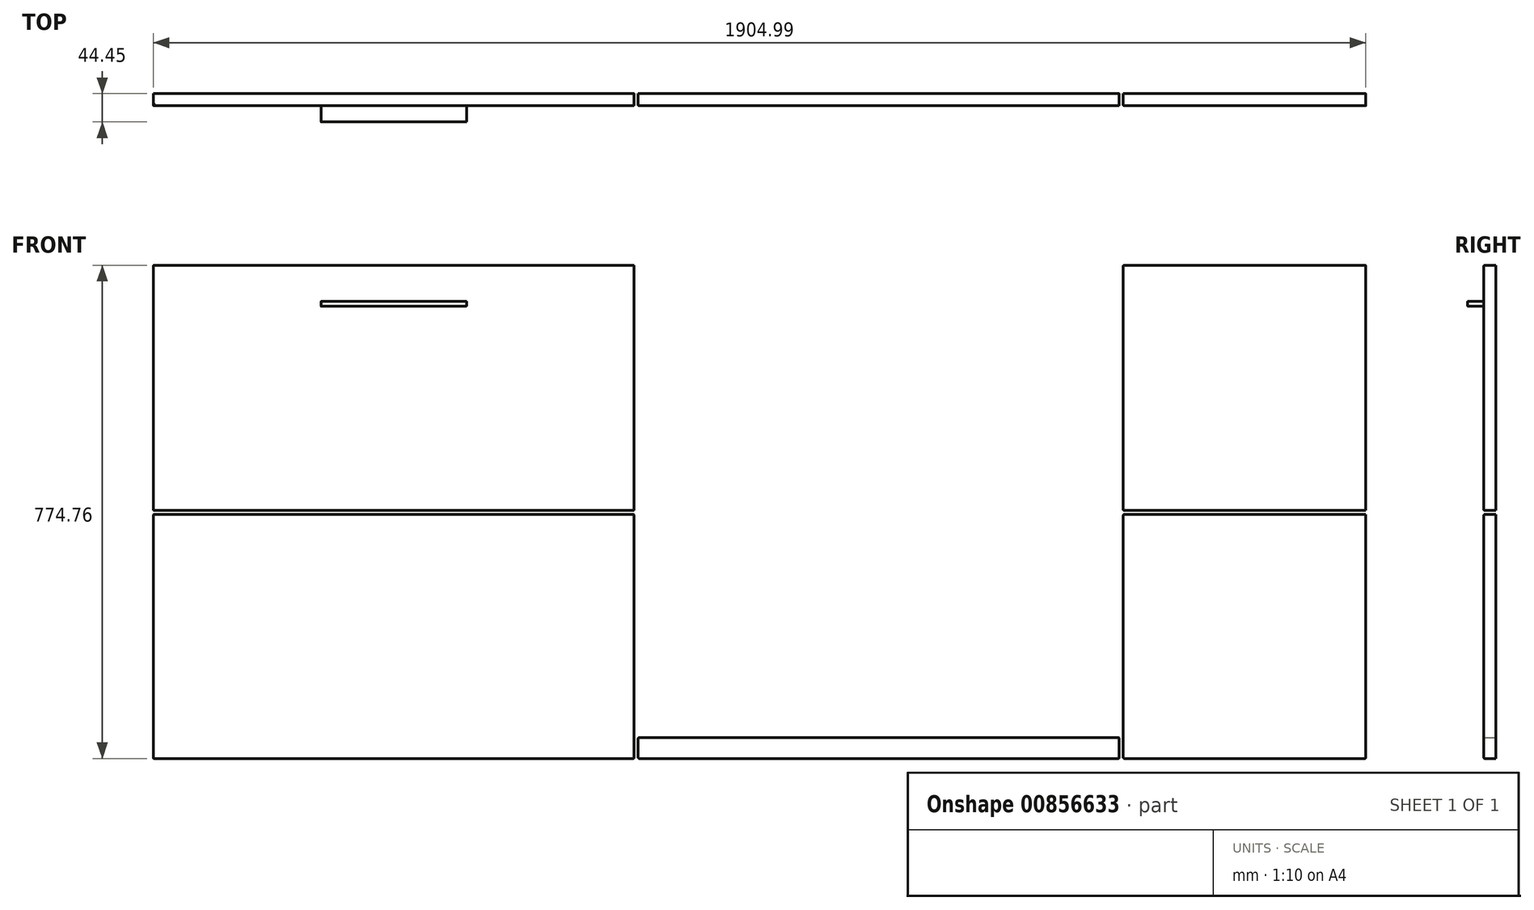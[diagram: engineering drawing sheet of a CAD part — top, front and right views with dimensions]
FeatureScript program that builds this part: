
annotation { "Feature Type Name" : "Feature", "Feature Type Description" : "" }
export const myFeature = defineFeature(function(context is Context, id is Id, definition is map)
    precondition{}
    {
        {
            var Q0;
            Q0=qCreatedBy(makeId("Front.planeOp"),FACE);
            var sketch = newSketch(context, id + "F0", { "sketchPlane" : qUnion([Q0])});
            skLineSegment(sketch, "E0.left", {"start": v(0, 0) * mm, "end": v(0.1, 863.6) * mm});
            skLineSegment(sketch, "E0.right", {"start": v(-1905, -2.15) * mm, "end": v(-1904.9, 861.45) * mm});
            skLineSegment(sketch, "E1.top", {"start": v(0.1, 901.7) * mm, "end": v(-2504.34, 901.7) * mm});
            skLineSegment(sketch, "E1.left", {"start": v(0.1, 863.6) * mm, "end": v(0.1, 901.7) * mm});
            skLineSegment(sketch, "E1.right", {"start": v(-2504.34, 863.6) * mm, "end": v(-2504.34, 901.7) * mm});
            skLineSegment(sketch, "E2", {"start": v(-1904.9, 1058.57) * mm, "end": v(-1904.9, -228.77) * mm, "construction": true});
            skLineSegment(sketch, "E3", {"start": v(0, 1058.57) * mm, "end": v(0, -228.77) * mm, "construction": true});
            skLineSegment(sketch, "E4.bottom", {"start": v(0, 0) * mm, "end": v(-381, 0) * mm});
            skLineSegment(sketch, "E4.left", {"start": v(0, 0) * mm, "end": v(0, 857.25) * mm});
            skLineSegment(sketch, "E5", {"start": v(-381, 0) * mm, "end": v(-387.35, 0) * mm, "construction": true});
            skLineSegment(sketch, "E6.bottom", {"start": v(-387.35, 0) * mm, "end": v(-1143, 0) * mm, "construction": true});
            skLineSegment(sketch, "E6.left", {"start": v(-387.35, 0) * mm, "end": v(-387.35, 736.6) * mm, "construction": true});
            skLineSegment(sketch, "E7", {"start": v(0, 0) * mm, "end": v(-1905, -2.15) * mm, "construction": true});
            skLineSegment(sketch, "E8.bottom", {"start": v(-387.35, 857.25) * mm, "end": v(-1143, 857.25) * mm, "construction": true});
            skLineSegment(sketch, "E8.top", {"start": v(-387.35, 121.5) * mm, "end": v(-1143, 120.65) * mm, "construction": true});
            skLineSegment(sketch, "E8.left", {"start": v(-387.35, 857.25) * mm, "end": v(-387.35, 121.5) * mm, "construction": true});
            skLineSegment(sketch, "E8.right", {"start": v(-1143, 857.25) * mm, "end": v(-1143, 120.65) * mm, "construction": true});
            skLineSegment(sketch, "E9", {"start": v(-1149.35, 857.25) * mm, "end": v(-1149.35, 120.65) * mm, "construction": true});
            skLineSegment(sketch, "E10.bottom", {"start": v(-1149.35, 857.25) * mm, "end": v(-1527.18, 857.25) * mm});
            skLineSegment(sketch, "E10.left", {"start": v(-1149.35, 857.25) * mm, "end": v(-1149.35, 82.55) * mm});
            skLineSegment(sketch, "E11.bottom", {"start": v(-1149.35, 82.5) * mm, "end": v(-1911.35, 82.5) * mm});
            skLineSegment(sketch, "E11.top", {"start": v(-1149.35, 857.25) * mm, "end": v(-1911.35, 857.25) * mm});
            skLineSegment(sketch, "E11.left", {"start": v(-1149.35, 82.5) * mm, "end": v(-1149.35, 857.25) * mm});
            skLineSegment(sketch, "E11.right", {"start": v(-1911.35, 82.5) * mm, "end": v(-1911.35, 857.25) * mm});
            skLineSegment(sketch, "E12", {"start": v(0, 857.25) * mm, "end": v(-2682.58, 857.25) * mm, "construction": true});
            skLineSegment(sketch, "E13.bottom", {"start": v(0, 857.25) * mm, "end": v(-381, 857.25) * mm});
            skLineSegment(sketch, "E13.top", {"start": v(0, 82.55) * mm, "end": v(-381, 82.55) * mm});
            skLineSegment(sketch, "E13.left", {"start": v(0, 857.25) * mm, "end": v(0, 82.55) * mm});
            skLineSegment(sketch, "E13.right", {"start": v(-381, 857.25) * mm, "end": v(-381, 82.55) * mm});
            skLineSegment(sketch, "E14.bottom", {"start": v(-387.35, 82.55) * mm, "end": v(-1143, 82.55) * mm});
            skLineSegment(sketch, "E14.top", {"start": v(-387.35, 115.22) * mm, "end": v(-1143, 115.22) * mm});
            skLineSegment(sketch, "E14.left", {"start": v(-387.35, 82.55) * mm, "end": v(-387.35, 115.22) * mm});
            skLineSegment(sketch, "E14.right", {"start": v(-1143, 82.55) * mm, "end": v(-1143, 115.22) * mm});
            skPoint(sketch, "E15", {"position": v(-765.18, 121.08) * mm});
            skSolve(sketch);
        }
        {
            var Q0;
            {var subQ0=sQuery(id+"F0.wireOp",EDGE,"E0.left");Q0=makeQuery(id+"F0.imprint","IMPRINT",FACE,{"disambiguationData":[TD([[makeQuery(id+"F0.imprint","IMPRINT",EDGE,{"derivedFrom":subQ0}),1.0]])]});}
            var Q1;
            Q1=makeQuery(id+"F0.imprint","IMPRINT",FACE,{"disambiguationData":[TD([[makeQuery(id+"F0.imprint","IMPRINT",EDGE,{"derivedFrom":sQuery(id+"F0.wireOp",EDGE,"E13.bottom")}),1.0]])]});
            var Q2;
            Q2=makeQuery(id+"F0.imprint","IMPRINT",FACE,{"disambiguationData":[TD([[makeQuery(id+"F0.imprint","IMPRINT",EDGE,{"derivedFrom":sQuery(id+"F0.wireOp",EDGE,"E10.bottom")}),1.0]])]});
            var Q3;
            {var subQ5=sQuery(id+"F0.wireOp",EDGE,"E11.left");Q3=makeQuery(id+"F0.imprint","IMPRINT",FACE,{"disambiguationData":[TD([[makeQuery(id+"F0.imprint","IMPRINT",EDGE,{"derivedFrom":subQ5}),1.0]])]});}
            var Q4;
            Q4=makeQuery(id+"F0.imprint","IMPRINT",FACE,{"disambiguationData":[TD([[makeQuery(id+"F0.imprint","IMPRINT",EDGE,{"derivedFrom":sQuery(id+"F0.wireOp",EDGE,"E14.bottom")}),-1.0]])]});
            extrude(context, id + "F1", {"entities" : qUnion([Q0, Q1, Q2, Q3, Q4]), "depth" : 19.05 * mm, "offsetDistance" : 25.4 * mm});
        }
        {
            var Q0;
            Q0=makeQuery(id+"F1.opExtrude","CAP_EDGE",EDGE,{"disambiguationData":[OSD([sQuery(id+"F0.wireOp",EDGE,"E10.bottom")])],"isStart":false});
            var Q1;
            Q1=makeQuery(id+"F1.opExtrude","SWEPT_EDGE",EDGE,{"disambiguationData":[OSD([sQuery(id+"F0.wireOp",EDGE,"E10.bottom"),sQuery(id+"F0.wireOp",EDGE,"E10.right")])]});
            var Q2;
            Q2=makeQuery(id+"F1.opExtrude","CAP_EDGE",EDGE,{"disambiguationData":[OSD([sQuery(id+"F0.wireOp",EDGE,"E10.right")])],"isStart":false});
            var Q3;
            Q3=makeQuery(id+"F1.opExtrude","SWEPT_EDGE",EDGE,{"disambiguationData":[OSD([sQuery(id+"F0.wireOp",EDGE,"E11.top"),sQuery(id+"F0.wireOp",EDGE,"E11.left")])]});
            var Q4;
            Q4=makeQuery(id+"F1.opExtrude","CAP_EDGE",EDGE,{"disambiguationData":[OSD([sQuery(id+"F0.wireOp",EDGE,"E11.left")])],"isStart":false});
            var Q5;
            Q5=makeQuery(id+"F1.opExtrude","CAP_EDGE",EDGE,{"disambiguationData":[OSD([sQuery(id+"F0.wireOp",EDGE,"E11.top")])],"isStart":false});
            var Q6;
            Q6=makeQuery(id+"F1.opExtrude","SWEPT_EDGE",EDGE,{"disambiguationData":[OSD([sQuery(id+"F0.wireOp",EDGE,"E0.right"),sQuery(id+"F0.wireOp",EDGE,"E11.top")])]});
            var Q7;
            Q7=makeQuery(id+"F1.opExtrude","CAP_EDGE",EDGE,{"disambiguationData":[OSD([sQuery(id+"F0.wireOp",EDGE,"E0.right")])],"isStart":false});
            var Q8;
            Q8=makeQuery(id+"F1.opExtrude","CAP_EDGE",EDGE,{"disambiguationData":[OSD([sQuery(id+"F0.wireOp",EDGE,"E11.bottom")])],"isStart":false});
            var Q9;
            Q9=makeQuery(id+"F1.opExtrude","CAP_EDGE",EDGE,{"disambiguationData":[OSD([sQuery(id+"F0.wireOp",EDGE,"E10.top")])],"isStart":false});
            var Q10;
            Q10=makeQuery(id+"F1.opExtrude","CAP_EDGE",EDGE,{"disambiguationData":[OSD([sQuery(id+"F0.wireOp",EDGE,"E10.left")])],"isStart":false});
            var Q11;
            Q11=makeQuery(id+"F1.opExtrude","SWEPT_EDGE",EDGE,{"disambiguationData":[OSD([sQuery(id+"F0.wireOp",EDGE,"E10.bottom"),sQuery(id+"F0.wireOp",EDGE,"E10.left")])]});
            var Q12;
            Q12=makeQuery(id+"F1.opExtrude","SWEPT_EDGE",EDGE,{"disambiguationData":[OSD([sQuery(id+"F0.wireOp",EDGE,"E11.bottom"),sQuery(id+"F0.wireOp",EDGE,"E11.left")])]});
            var Q13;
            Q13=makeQuery(id+"F1.opExtrude","SWEPT_EDGE",EDGE,{"disambiguationData":[OSD([sQuery(id+"F0.wireOp",EDGE,"E10.top"),sQuery(id+"F0.wireOp",EDGE,"E10.left")])]});
            var Q14;
            Q14=makeQuery(id+"F1.opExtrude","SWEPT_EDGE",EDGE,{"disambiguationData":[OSD([sQuery(id+"F0.wireOp",EDGE,"E10.top"),sQuery(id+"F0.wireOp",EDGE,"E10.right")])]});
            var Q15;
            Q15=makeQuery(id+"F1.opExtrude","SWEPT_EDGE",EDGE,{"disambiguationData":[OSD([sQuery(id+"F0.wireOp",EDGE,"E14.bottom"),sQuery(id+"F0.wireOp",EDGE,"E14.right")])]});
            var Q16;
            Q16=makeQuery(id+"F1.opExtrude","SWEPT_EDGE",EDGE,{"disambiguationData":[OSD([sQuery(id+"F0.wireOp",EDGE,"E14.top"),sQuery(id+"F0.wireOp",EDGE,"E14.right")])]});
            var Q17;
            Q17=makeQuery(id+"F1.opExtrude","CAP_EDGE",EDGE,{"disambiguationData":[OSD([sQuery(id+"F0.wireOp",EDGE,"E14.right")])],"isStart":false});
            var Q18;
            Q18=makeQuery(id+"F1.opExtrude","CAP_EDGE",EDGE,{"disambiguationData":[OSD([sQuery(id+"F0.wireOp",EDGE,"E14.bottom")])],"isStart":false});
            var Q19;
            Q19=makeQuery(id+"F1.opExtrude","CAP_EDGE",EDGE,{"disambiguationData":[OSD([sQuery(id+"F0.wireOp",EDGE,"E14.top")])],"isStart":false});
            var Q20;
            Q20=makeQuery(id+"F1.opExtrude","SWEPT_EDGE",EDGE,{"disambiguationData":[OSD([sQuery(id+"F0.wireOp",EDGE,"E14.top"),sQuery(id+"F0.wireOp",EDGE,"E14.left")])]});
            var Q21;
            Q21=makeQuery(id+"F1.opExtrude","SWEPT_EDGE",EDGE,{"disambiguationData":[OSD([sQuery(id+"F0.wireOp",EDGE,"E14.bottom"),sQuery(id+"F0.wireOp",EDGE,"E14.left")])]});
            var Q22;
            Q22=makeQuery(id+"F1.opExtrude","SWEPT_EDGE",EDGE,{"disambiguationData":[OSD([sQuery(id+"F0.wireOp",EDGE,"E13.top"),sQuery(id+"F0.wireOp",EDGE,"E13.right")])]});
            var Q23;
            Q23=makeQuery(id+"F1.opExtrude","CAP_EDGE",EDGE,{"disambiguationData":[OSD([sQuery(id+"F0.wireOp",EDGE,"E14.left")])],"isStart":false});
            var Q24;
            Q24=makeQuery(id+"F1.opExtrude","CAP_EDGE",EDGE,{"disambiguationData":[OSD([sQuery(id+"F0.wireOp",EDGE,"E13.right")])],"isStart":false});
            var Q25;
            Q25=makeQuery(id+"F1.opExtrude","CAP_EDGE",EDGE,{"disambiguationData":[OSD([sQuery(id+"F0.wireOp",EDGE,"E13.top")])],"isStart":false});
            var Q26;
            Q26=makeQuery(id+"F1.opExtrude","SWEPT_EDGE",EDGE,{"disambiguationData":[OSD([sQuery(id+"F0.wireOp",EDGE,"E13.top"),sQuery(id+"F0.wireOp",EDGE,"E13.left")])]});
            var Q27;
            Q27=makeQuery(id+"F1.opExtrude","SWEPT_EDGE",EDGE,{"disambiguationData":[OSD([sQuery(id+"F0.wireOp",EDGE,"E13.bottom"),sQuery(id+"F0.wireOp",EDGE,"E13.left")])]});
            var Q28;
            Q28=makeQuery(id+"F1.opExtrude","CAP_EDGE",EDGE,{"disambiguationData":[OSD([sQuery(id+"F0.wireOp",EDGE,"E13.bottom")])],"isStart":false});
            var Q29;
            Q29=makeQuery(id+"F1.opExtrude","CAP_EDGE",EDGE,{"disambiguationData":[OSD([sQuery(id+"F0.wireOp",EDGE,"E13.left")])],"isStart":false});
            var Q30;
            Q30=makeQuery(id+"F1.opExtrude","SWEPT_EDGE",EDGE,{"disambiguationData":[OSD([sQuery(id+"F0.wireOp",EDGE,"E13.bottom"),sQuery(id+"F0.wireOp",EDGE,"E13.right")])]});
            var Q31;
            Q31=makeQuery(id+"F1.opExtrude","SWEPT_EDGE",EDGE,{"disambiguationData":[OSD([sQuery(id+"F0.wireOp",EDGE,"E0.right"),sQuery(id+"F0.wireOp",EDGE,"E11.bottom")])]});
            fillet(context, id + "F2", {"entities" : qUnion([Q0, Q1, Q2, Q3, Q4, Q5, Q6, Q7, Q8, Q9, Q10, Q11, Q12, Q13, Q14, Q15, Q16, Q17, Q18, Q19, Q20, Q21, Q22, Q23, Q24, Q25, Q26, Q27, Q28, Q29, Q30, Q31]), "radius" : 1.27 * mm, "tangentPropagation" : true, "allowEdgeOverflow" : false});
        }
        {
            var Q0;
            Q0=makeQuery(id+"F1.opExtrude","CAP_FACE",FACE,{"disambiguationData":[OSD([sQuery(id+"F0.wireOp",EDGE,"E0.right"),sQuery(id+"F0.wireOp",EDGE,"E11.bottom"),sQuery(id+"F0.wireOp",EDGE,"E11.top"),sQuery(id+"F0.wireOp",EDGE,"E11.left")])],"isStart":false});
            var sketch = newSketch(context, id + "F3", { "sketchPlane" : qUnion([Q0])});
            skLineSegment(sketch, "E16.bottom", {"start": v(-1412.83, 792.8) * mm, "end": v(-1641.43, 792.8) * mm});
            skLineSegment(sketch, "E16.top", {"start": v(-1412.83, 800.41) * mm, "end": v(-1641.43, 800.41) * mm});
            skLineSegment(sketch, "E16.left", {"start": v(-1412.83, 792.8) * mm, "end": v(-1412.83, 800.41) * mm});
            skLineSegment(sketch, "E16.right", {"start": v(-1641.43, 792.8) * mm, "end": v(-1641.43, 800.41) * mm});
            skPoint(sketch, "E16.middle", {"position": v(-1527.13, 796.6) * mm});
            skPoint(sketch, "E16.middle.positionSnap0", {"position": v(-1527.13, 855.98) * mm});
            skPoint(sketch, "E16.centerSnap0", {"position": v(-1527.13, 855.98) * mm});
            skSolve(sketch);
        }
        {
            var Q0;
            Q0 = qSketchRegion(id + "F3", true);
            extrude(context, id + "F4", {"entities" : qUnion([Q0]), "depth" : 25.4 * mm, "offsetDistance" : 25.4 * mm});
        }
        {
            var Q0;
            Q0=makeQuery(id+"F4.opExtrude","CAP_FACE",FACE,{"disambiguationData":[OSD([sQuery(id+"F3.wireOp",EDGE,"E16.bottom"),sQuery(id+"F3.wireOp",EDGE,"E16.top"),sQuery(id+"F3.wireOp",EDGE,"E16.left"),sQuery(id+"F3.wireOp",EDGE,"E16.right")])],"isStart":false});
            var Q1;
            Q1=makeQuery(id+"F4.opExtrude","SWEPT_EDGE",EDGE,{"disambiguationData":[OSD([sQuery(id+"F3.wireOp",EDGE,"E16.top"),sQuery(id+"F3.wireOp",EDGE,"E16.right")])]});
            var Q2;
            Q2=makeQuery(id+"F4.opExtrude","SWEPT_EDGE",EDGE,{"disambiguationData":[OSD([sQuery(id+"F3.wireOp",EDGE,"E16.bottom"),sQuery(id+"F3.wireOp",EDGE,"E16.right")])]});
            var Q3;
            Q3=makeQuery(id+"F4.opExtrude","CAP_EDGE",EDGE,{"disambiguationData":[OSD([sQuery(id+"F3.wireOp",EDGE,"E16.top")])],"isStart":true});
            var Q4;
            Q4=makeQuery(id+"F4.opExtrude","CAP_EDGE",EDGE,{"disambiguationData":[OSD([sQuery(id+"F3.wireOp",EDGE,"E16.right")])],"isStart":true});
            var Q5;
            Q5=makeQuery(id+"F4.opExtrude","CAP_EDGE",EDGE,{"disambiguationData":[OSD([sQuery(id+"F3.wireOp",EDGE,"E16.bottom")])],"isStart":true});
            var Q6;
            Q6=makeQuery(id+"F4.opExtrude","SWEPT_EDGE",EDGE,{"disambiguationData":[OSD([sQuery(id+"F3.wireOp",EDGE,"E16.bottom"),sQuery(id+"F3.wireOp",EDGE,"E16.left")])]});
            var Q7;
            Q7=makeQuery(id+"F4.opExtrude","SWEPT_EDGE",EDGE,{"disambiguationData":[OSD([sQuery(id+"F3.wireOp",EDGE,"E16.top"),sQuery(id+"F3.wireOp",EDGE,"E16.left")])]});
            var Q8;
            Q8=makeQuery(id+"F4.opExtrude","CAP_EDGE",EDGE,{"disambiguationData":[OSD([sQuery(id+"F3.wireOp",EDGE,"E16.left")])],"isStart":true});
            fillet(context, id + "F5", {"entities" : qUnion([Q0, Q1, Q2, Q3, Q4, Q5, Q6, Q7, Q8]), "radius" : 0.32 * mm, "tangentPropagation" : true, "allowEdgeOverflow" : false});
        }
        {
            var Q0;
            Q0=makeQuery(id+"F1.opExtrude","CAP_FACE",FACE,{"disambiguationData":[OSD([sQuery(id+"F0.wireOp",EDGE,"E0.right"),sQuery(id+"F0.wireOp",EDGE,"E11.bottom"),sQuery(id+"F0.wireOp",EDGE,"E11.top"),sQuery(id+"F0.wireOp",EDGE,"E11.left")])],"isStart":false});
            var sketch = newSketch(context, id + "F6", { "sketchPlane" : qUnion([Q0])});
            skLineSegment(sketch, "E17", {"start": v(-1903.63, 855.98) * mm, "end": v(-1903.63, 856.22) * mm, "construction": true});
            skLineSegment(sketch, "E18", {"start": v(-1903.63, 856.22) * mm, "end": v(-1903.87, 856.22) * mm, "construction": true});
            skLineSegment(sketch, "E19", {"start": v(-1903.63, 855.98) * mm, "end": v(-1903.87, 855.98) * mm, "construction": true});
            skLineSegment(sketch, "E20", {"start": v(-1903.87, 855.98) * mm, "end": v(-1903.87, 856.22) * mm, "construction": true});
            skLineSegment(sketch, "E21", {"start": v(-1903.87, 856.22) * mm, "end": v(-1759.66, 856.22) * mm, "construction": true});
            skLineSegment(sketch, "E22.bottom", {"start": v(-1911.27, 472.05) * mm, "end": v(120.73, 472.05) * mm});
            skLineSegment(sketch, "E22.top", {"start": v(-1911.27, 465.7) * mm, "end": v(120.73, 465.7) * mm});
            skLineSegment(sketch, "E22.left", {"start": v(-1911.27, 472.05) * mm, "end": v(-1911.27, 465.7) * mm});
            skLineSegment(sketch, "E22.right", {"start": v(120.73, 472.05) * mm, "end": v(120.73, 465.7) * mm});
            skSolve(sketch);
        }
        {
            var Q0;
            Q0 = qSketchRegion(id + "F6", true);
            extrude(context, id + "F7", {"entities" : qUnion([Q0]), "operationType" : NewBodyOperationType.REMOVE, "oppositeDirection" : true, "depth" : 25.4 * mm, "offsetDistance" : 25.4 * mm});
        }
        {
            var Q0;
            Q0=makeQuery(id+"F7.boolean.opBoolean","INTERSECT",EDGE,{"derivedFrom":[makeQuery(id+"F1.opExtrude","SWEPT_FACE",FACE,{"disambiguationData":[OSD([sQuery(id+"F0.wireOp",EDGE,"E0.right")])]}),makeQuery(id+"F7.opExtrude","SWEPT_FACE",FACE,{"disambiguationData":[OSD([sQuery(id+"F6.wireOp",EDGE,"E22.bottom")])]})]});
            var Q1;
            Q1=makeQuery(id+"F7.boolean.opBoolean","INTERSECT",EDGE,{"derivedFrom":[makeQuery(id+"F1.opExtrude","SWEPT_FACE",FACE,{"disambiguationData":[OSD([sQuery(id+"F0.wireOp",EDGE,"E0.right")])]}),makeQuery(id+"F7.opExtrude","SWEPT_FACE",FACE,{"disambiguationData":[OSD([sQuery(id+"F6.wireOp",EDGE,"E22.top")])]})]});
            var Q2;
            Q2=makeQuery(id+"F7.boolean.opBoolean","INTERSECT",EDGE,{"derivedFrom":[makeQuery(id+"F1.opExtrude","SWEPT_FACE",FACE,{"disambiguationData":[OSD([sQuery(id+"F0.wireOp",EDGE,"E13.right")])]}),makeQuery(id+"F7.opExtrude","SWEPT_FACE",FACE,{"disambiguationData":[OSD([sQuery(id+"F6.wireOp",EDGE,"E22.bottom")])]})]});
            var Q3;
            Q3=makeQuery(id+"F7.boolean.opBoolean","INTERSECT",EDGE,{"derivedFrom":[makeQuery(id+"F1.opExtrude","SWEPT_FACE",FACE,{"disambiguationData":[OSD([sQuery(id+"F0.wireOp",EDGE,"E13.right")])]}),makeQuery(id+"F7.opExtrude","SWEPT_FACE",FACE,{"disambiguationData":[OSD([sQuery(id+"F6.wireOp",EDGE,"E22.top")])]})]});
            fillet(context, id + "F8", {"entities" : qUnion([Q0, Q1, Q2, Q3]), "radius" : 1.27 * mm, "tangentPropagation" : true, "allowEdgeOverflow" : false});
        }
    });
